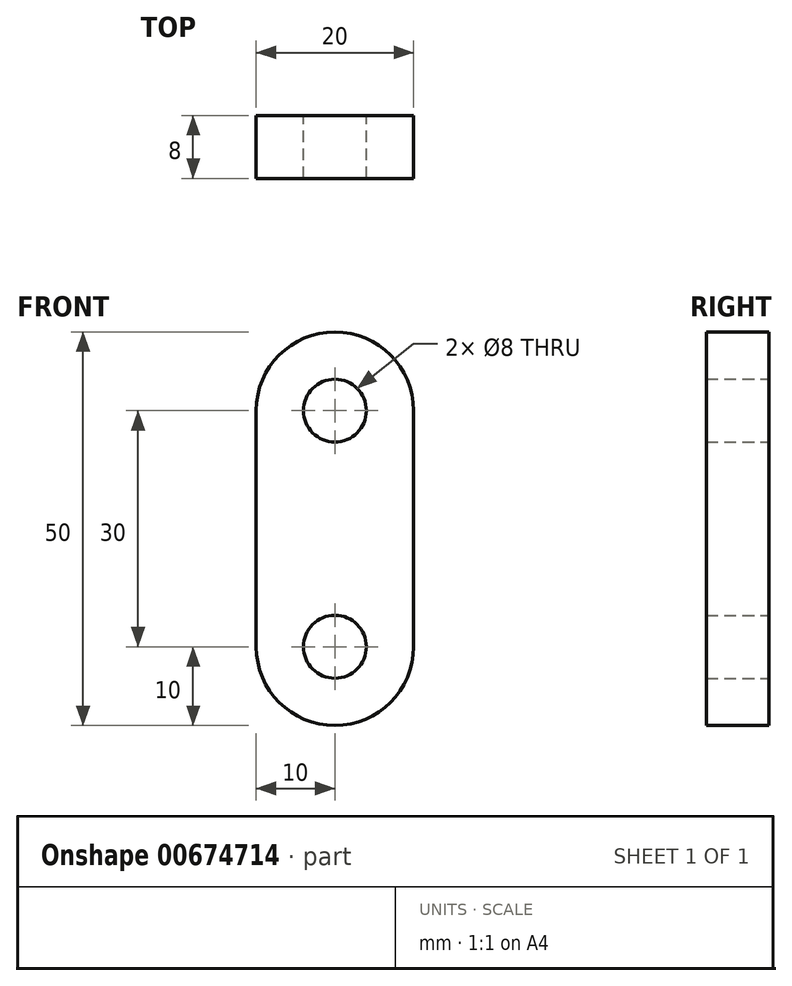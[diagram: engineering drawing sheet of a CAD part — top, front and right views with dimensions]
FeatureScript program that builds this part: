
annotation { "Feature Type Name" : "Feature", "Feature Type Description" : "" }
export const myFeature = defineFeature(function(context is Context, id is Id, definition is map)
    precondition{}
    {
        {
            var Q0;
            Q0=qCreatedBy(makeId("Front.planeOp"),FACE);
            var sketch = newSketch(context, id + "F0", { "sketchPlane" : qUnion([Q0])});
            skArc(sketch, "E0", {"start": v(-10, 0) * mm, "mid": v(0, -10) * mm, "end": v(10, 0) * mm});
            skArc(sketch, "E1", {"start": v(10, 30) * mm, "mid": v(0, 40) * mm, "end": v(-10, 30) * mm});
            skCircle(sketch, "E2", {"center": v(0, 30) * mm, "radius": 4 * mm});
            skCircle(sketch, "E3", {"center": v(0, 0) * mm, "radius": 4 * mm});
            skLineSegment(sketch, "E4", {"start": v(-10, 30) * mm, "end": v(-10, 0) * mm});
            skLineSegment(sketch, "E5", {"start": v(10, 30) * mm, "end": v(10, 0) * mm});
            skSolve(sketch);
        }
        {
            var Q0;
            Q0 = qSketchRegion(id + "F0", true);
            extrude(context, id + "F1", {"entities" : qUnion([Q0]), "depth" : 8 * mm, "offsetDistance" : 25 * mm});
        }
    });
